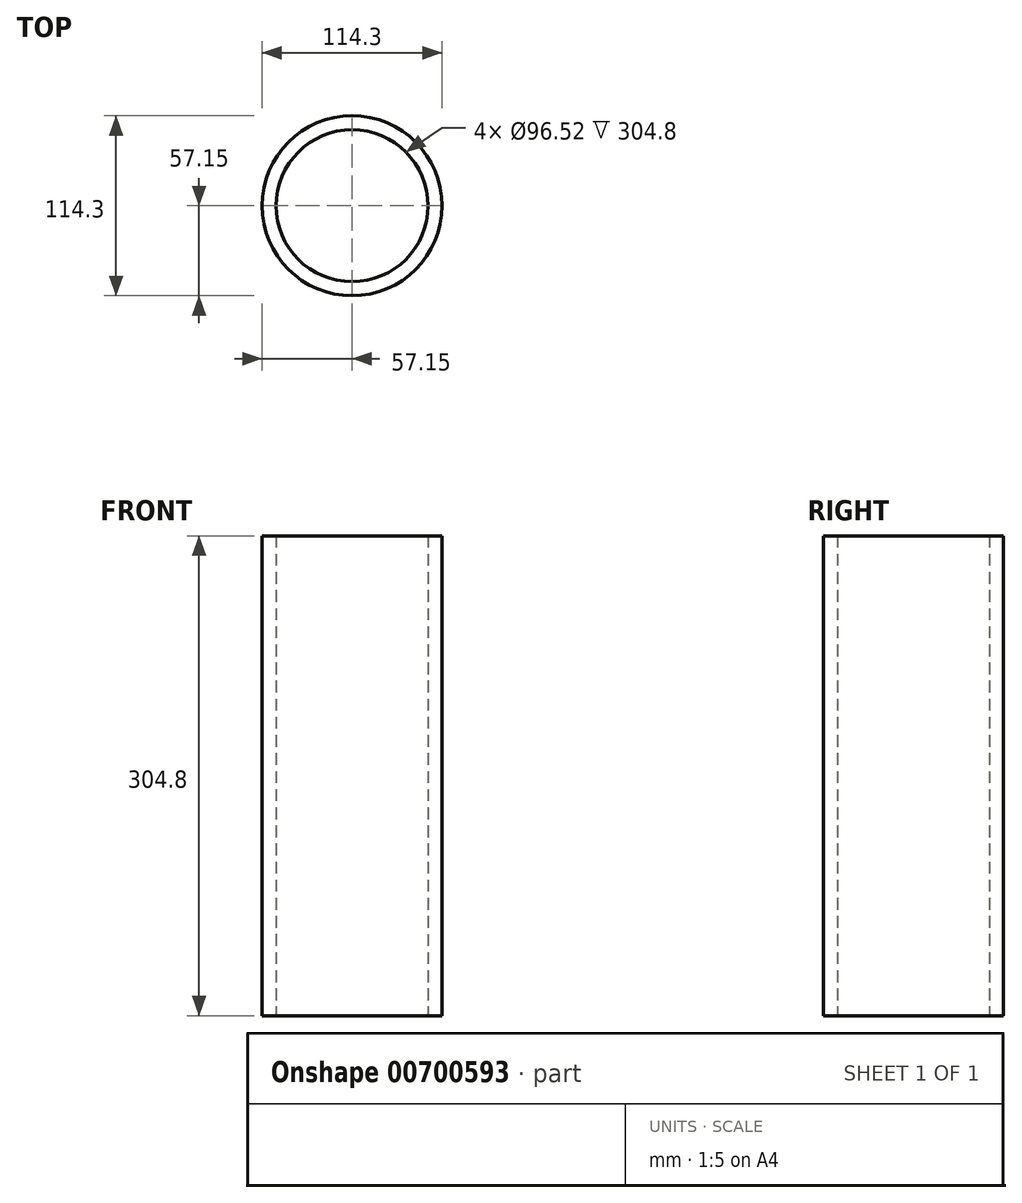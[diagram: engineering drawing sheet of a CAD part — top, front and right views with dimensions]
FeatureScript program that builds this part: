
annotation { "Feature Type Name" : "Feature", "Feature Type Description" : "" }
export const myFeature = defineFeature(function(context is Context, id is Id, definition is map)
    precondition{}
    {
        {
            var Q0;
            Q0=qCreatedBy(makeId("Top.planeOp"),FACE);
            var sketch = newSketch(context, id + "F0", { "sketchPlane" : qUnion([Q0])});
            skCircle(sketch, "E0", {"center": v(0, 0) * mm, "radius": 57.15 * mm});
            skCircle(sketch, "E1", {"center": v(0, 0) * mm, "radius": 48.26 * mm});
            skSolve(sketch);
        }
        {
            var Q0;
            Q0 = qSketchRegion(id + "F0", true);
            extrude(context, id + "F1", {"entities" : qUnion([Q0]), "depth" : 304.8 * mm, "offsetDistance" : 25.4 * mm});
        }
    });
